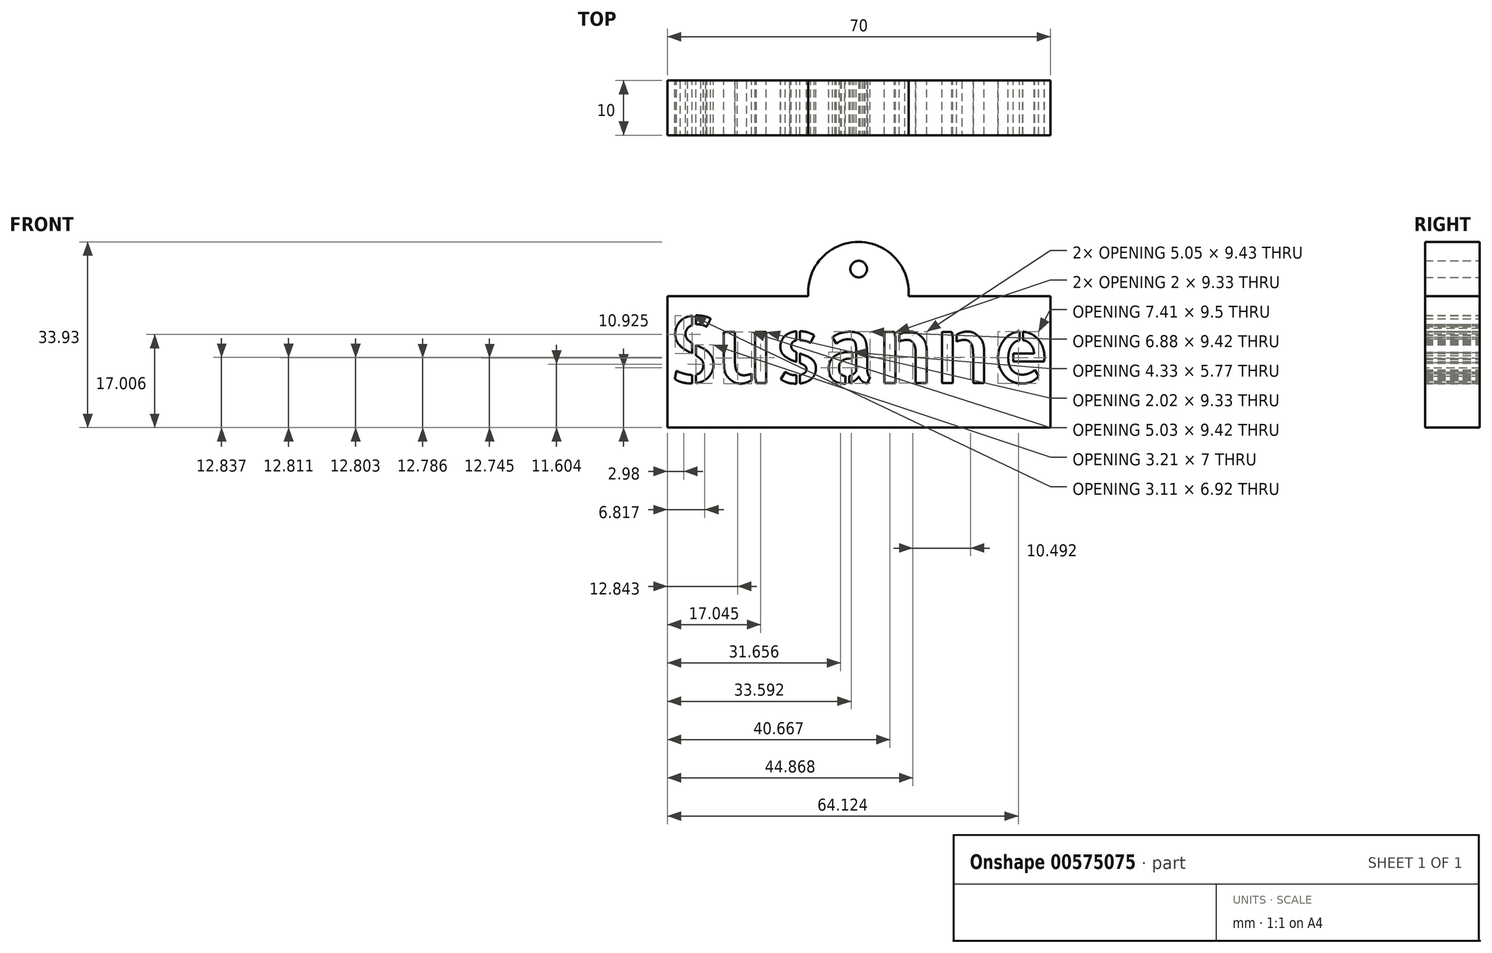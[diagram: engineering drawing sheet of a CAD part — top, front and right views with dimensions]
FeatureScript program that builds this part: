
annotation { "Feature Type Name" : "Feature", "Feature Type Description" : "" }
export const myFeature = defineFeature(function(context is Context, id is Id, definition is map)
    precondition{}
    {
        {
            var Q0;
            Q0=qCreatedBy(makeId("Front.planeOp"),FACE);
            var sketch = newSketch(context, id + "F0", { "sketchPlane" : qUnion([Q0])});
            skLineSegment(sketch, "E0.bottom", {"start": v(-61.9, 29.86) * mm, "end": v(8.1, 29.86) * mm});
            skLineSegment(sketch, "E0.top", {"start": v(-61.9, 5.86) * mm, "end": v(8.1, 5.86) * mm});
            skLineSegment(sketch, "E0.left", {"start": v(-61.9, 29.86) * mm, "end": v(-61.9, 5.86) * mm});
            skLineSegment(sketch, "E0.right", {"start": v(8.1, 29.86) * mm, "end": v(8.1, 5.86) * mm});
            skPoint(sketch, "E1", {"position": v(-26.9, 29.86) * mm});
            skArc(sketch, "E2", {"start": v(-17.84, 29.86) * mm, "mid": v(-27, 39.79) * mm, "end": v(-36.16, 29.86) * mm});
            skPoint(sketch, "E3", {"position": v(-27, 39.79) * mm});
            skCircle(sketch, "E4", {"center": v(-26.95, 34.83) * mm, "radius": 1.52 * mm});
            skText(sketch, "E5", { "text": "Susanne\n", "fontName": "AllertaStencil-Regular.ttf"});
            const initialGuessF0  = {"E5": [-0.0619, 0.01398, 1, 0, 0.0122]};
            skSetInitialGuess(sketch, initialGuessF0);
            skSolve(sketch);
        }
        {
            var Q0;
            Q0 = qSketchRegion(id + "F0", true);
            extrude(context, id + "F1", {"entities" : qUnion([Q0]), "depth" : 10 * mm, "offsetDistance" : 25 * mm});
        }
    });
